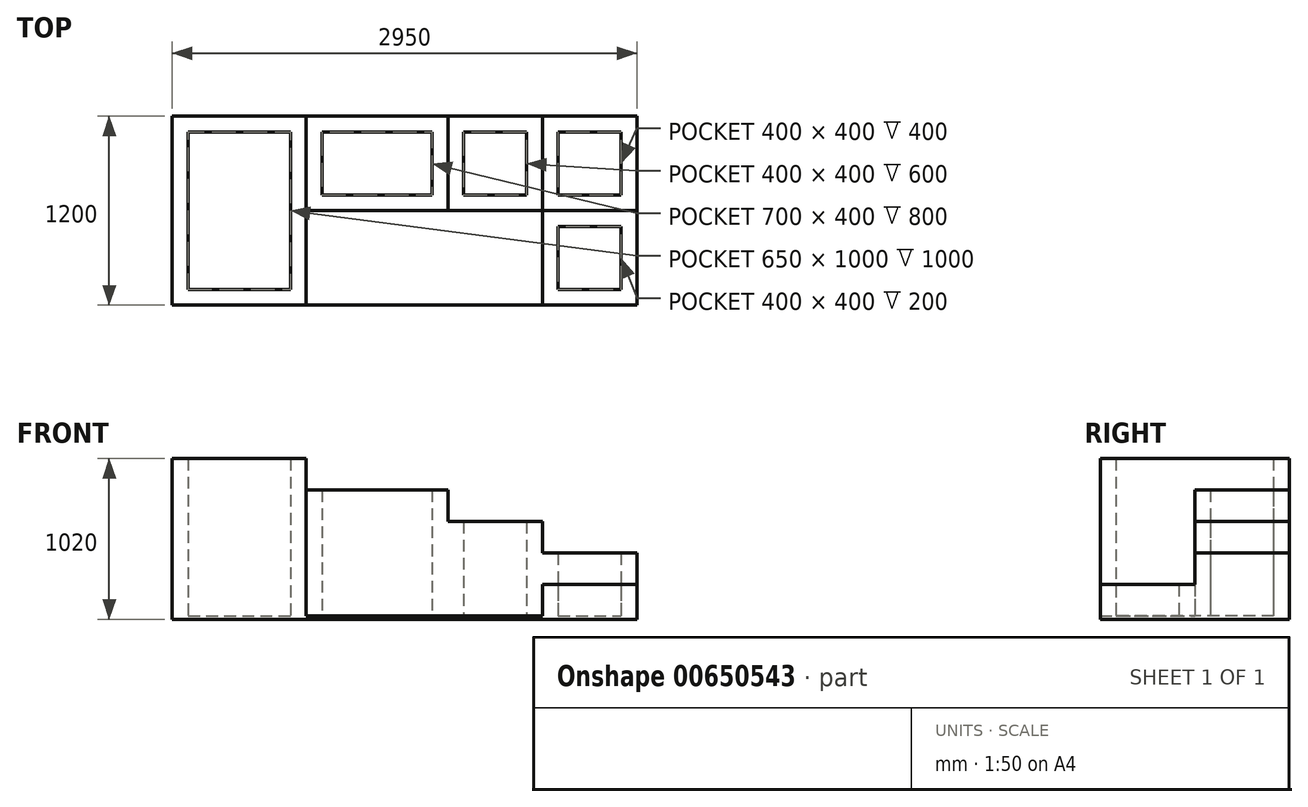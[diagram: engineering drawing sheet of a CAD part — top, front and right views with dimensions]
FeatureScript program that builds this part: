
annotation { "Feature Type Name" : "Feature", "Feature Type Description" : "" }
export const myFeature = defineFeature(function(context is Context, id is Id, definition is map)
    precondition{}
    {
        {
            var Q0;
            Q0=qCreatedBy(makeId("Top.planeOp"),FACE);
            var sketch = newSketch(context, id + "F0", { "sketchPlane" : qUnion([Q0])});
            skLineSegment(sketch, "E0.bottom", {"start": v(0, 0) * mm, "end": v(-2563.64, 0) * mm});
            skLineSegment(sketch, "E0.top", {"start": v(0, 1200) * mm, "end": v(-2950, 1200) * mm});
            skLineSegment(sketch, "E0.left", {"start": v(0, 0) * mm, "end": v(0, 1200) * mm});
            skLineSegment(sketch, "E0.right", {"start": v(-2950, 0) * mm, "end": v(-2950, 1200) * mm});
            skLineSegment(sketch, "E1", {"start": v(-2563.64, 0) * mm, "end": v(-2950, 0) * mm});
            skSolve(sketch);
        }
        {
            var Q0;
            Q0=makeQuery(id+"F0.imprint","IMPRINT",FACE,{"disambiguationData":[TD([[makeQuery(id+"F0.imprint","IMPRINT",EDGE,{"derivedFrom":sQuery(id+"F0.wireOp",EDGE,"E0.bottom")}),-1.0]])]});
            extrude(context, id + "F1", {"entities" : qUnion([Q0]), "depth" : 20 * mm, "offsetDistance" : 25 * mm});
        }
        {
            var Q0;
            Q0=makeQuery(id+"F1.opExtrude","CAP_FACE",FACE,{"disambiguationData":[OSD([sQuery(id+"F0.wireOp",EDGE,"E0.bottom"),sQuery(id+"F0.wireOp",EDGE,"E0.top"),sQuery(id+"F0.wireOp",EDGE,"E0.left"),sQuery(id+"F0.wireOp",EDGE,"E0.right"),sQuery(id+"F0.wireOp",EDGE,"EcOLhzoJ-yrHA-FEvU-6dDI-CAjuHtf4V0fh.bottom"),sQuery(id+"F0.wireOp",EDGE,"EcOLhzoJ-yrHA-FEvU-6dDI-CAjuHtf4V0fh.top"),sQuery(id+"F0.wireOp",EDGE,"EcOLhzoJ-yrHA-FEvU-6dDI-CAjuHtf4V0fh.left"),sQuery(id+"F0.wireOp",EDGE,"EcOLhzoJ-yrHA-FEvU-6dDI-CAjuHtf4V0fh.right")])],"isStart":false});
            var sketch = newSketch(context, id + "F2", { "sketchPlane" : qUnion([Q0])});
            skLineSegment(sketch, "E2.bottom", {"start": v(0, 1200) * mm, "end": v(-600, 1200) * mm});
            skLineSegment(sketch, "E2.top", {"start": v(0, 600) * mm, "end": v(-600, 600) * mm});
            skLineSegment(sketch, "E2.left", {"start": v(0, 1200) * mm, "end": v(0, 600) * mm});
            skLineSegment(sketch, "E2.right", {"start": v(-600, 1200) * mm, "end": v(-600, 600) * mm});
            skLineSegment(sketch, "E3.bottom", {"start": v(-500, 1100) * mm, "end": v(-100, 1100) * mm});
            skLineSegment(sketch, "E3.top", {"start": v(-500, 700) * mm, "end": v(-100, 700) * mm});
            skLineSegment(sketch, "E3.left", {"start": v(-500, 1100) * mm, "end": v(-500, 700) * mm});
            skLineSegment(sketch, "E3.right", {"start": v(-100, 1100) * mm, "end": v(-100, 700) * mm});
            skSolve(sketch);
        }
        {
            var Q0;
            Q0=qSketchRegion(id+"F2",true);
            extrude(context, id + "F3", {"entities" : qUnion([Q0]), "operationType" : NewBodyOperationType.ADD, "depth" : 400 * mm, "offsetDistance" : 25 * mm});
        }
        {
            var Q0;
            {var subQ0=sQuery(id+"F0.wireOp",EDGE,"E0.left");var subQ1=sQuery(id+"F0.wireOp",EDGE,"EcOLhzoJ-yrHA-FEvU-6dDI-CAjuHtf4V0fh.right");var subQ2=sQuery(id+"F0.wireOp",EDGE,"EcOLhzoJ-yrHA-FEvU-6dDI-CAjuHtf4V0fh.left");var subQ3=sQuery(id+"F0.wireOp",EDGE,"EcOLhzoJ-yrHA-FEvU-6dDI-CAjuHtf4V0fh.top");var subQ4=sQuery(id+"F0.wireOp",EDGE,"EcOLhzoJ-yrHA-FEvU-6dDI-CAjuHtf4V0fh.bottom");var subQ5=sQuery(id+"F0.wireOp",EDGE,"E0.bottom");var subQ6=sQuery(id+"F0.wireOp",EDGE,"E0.right");var subQ7=sQuery(id+"F0.wireOp",EDGE,"E0.top");Q0=makeQuery(id+"F3.boolean.opBoolean","SPLIT",FACE,{"disambiguationData":[TD([makeQuery(id+"F1.opExtrude","SWEPT_FACE",FACE,{"disambiguationData":[OSD([subQ5])]})])],"derivedFrom":makeQuery(id+"F1.opExtrude","CAP_FACE",FACE,{"disambiguationData":[OSD([subQ5,subQ7,subQ0,subQ6,subQ4,subQ3,subQ2,subQ1])],"isStart":false})});}
            var sketch = newSketch(context, id + "F4", { "sketchPlane" : qUnion([Q0])});
            skLineSegment(sketch, "E4.bottom", {"start": v(-600, 600) * mm, "end": v(-1200, 600) * mm});
            skLineSegment(sketch, "E4.top", {"start": v(-600, 1200) * mm, "end": v(-1200, 1200) * mm});
            skLineSegment(sketch, "E4.left", {"start": v(-600, 600) * mm, "end": v(-600, 1200) * mm});
            skLineSegment(sketch, "E4.right", {"start": v(-1200, 600) * mm, "end": v(-1200, 1200) * mm});
            skLineSegment(sketch, "E5.bottom", {"start": v(-700, 700) * mm, "end": v(-1100, 700) * mm});
            skLineSegment(sketch, "E5.top", {"start": v(-700, 1100) * mm, "end": v(-1100, 1100) * mm});
            skLineSegment(sketch, "E5.left", {"start": v(-700, 700) * mm, "end": v(-700, 1100) * mm});
            skLineSegment(sketch, "E5.right", {"start": v(-1100, 700) * mm, "end": v(-1100, 1100) * mm});
            skSolve(sketch);
        }
        {
            var Q0;
            Q0=qSketchRegion(id+"F4",true);
            extrude(context, id + "F5", {"entities" : qUnion([Q0]), "operationType" : NewBodyOperationType.ADD, "depth" : 600 * mm, "offsetDistance" : 25 * mm});
        }
        {
            var Q0;
            {var subQ1=sQuery(id+"F0.wireOp",EDGE,"E0.left");var subQ3=sQuery(id+"F0.wireOp",EDGE,"EcOLhzoJ-yrHA-FEvU-6dDI-CAjuHtf4V0fh.right");var subQ5=sQuery(id+"F0.wireOp",EDGE,"EcOLhzoJ-yrHA-FEvU-6dDI-CAjuHtf4V0fh.left");var subQ8=sQuery(id+"F0.wireOp",EDGE,"EcOLhzoJ-yrHA-FEvU-6dDI-CAjuHtf4V0fh.top");var subQ11=sQuery(id+"F0.wireOp",EDGE,"EcOLhzoJ-yrHA-FEvU-6dDI-CAjuHtf4V0fh.bottom");var subQ13=sQuery(id+"F0.wireOp",EDGE,"E0.bottom");var subQ14=makeQuery(id+"F1.opExtrude","SWEPT_FACE",FACE,{"disambiguationData":[OSD([subQ13])]});var subQ15=sQuery(id+"F0.wireOp",EDGE,"E0.right");var subQ17=sQuery(id+"F0.wireOp",EDGE,"E0.top");Q0=makeQuery(id+"F5.boolean.opBoolean","SPLIT",FACE,{"disambiguationData":[TD([subQ14])],"derivedFrom":makeQuery(id+"F3.boolean.opBoolean","SPLIT",FACE,{"disambiguationData":[TD([subQ14])],"derivedFrom":makeQuery(id+"F1.opExtrude","CAP_FACE",FACE,{"disambiguationData":[OSD([subQ13,subQ17,subQ1,subQ15,subQ11,subQ8,subQ5,subQ3])],"isStart":false})})});}
            var sketch = newSketch(context, id + "F6", { "sketchPlane" : qUnion([Q0])});
            skLineSegment(sketch, "E6.bottom", {"start": v(-1200, 600) * mm, "end": v(-2100, 600) * mm});
            skLineSegment(sketch, "E6.top", {"start": v(-1200, 1200) * mm, "end": v(-2100, 1200) * mm});
            skLineSegment(sketch, "E6.left", {"start": v(-1200, 600) * mm, "end": v(-1200, 1200) * mm});
            skLineSegment(sketch, "E6.right", {"start": v(-2100, 600) * mm, "end": v(-2100, 1200) * mm});
            skLineSegment(sketch, "E7.bottom", {"start": v(-1300, 700) * mm, "end": v(-2000, 700) * mm});
            skLineSegment(sketch, "E7.top", {"start": v(-1300, 1100) * mm, "end": v(-2000, 1100) * mm});
            skLineSegment(sketch, "E7.left", {"start": v(-1300, 700) * mm, "end": v(-1300, 1100) * mm});
            skLineSegment(sketch, "E7.right", {"start": v(-2000, 700) * mm, "end": v(-2000, 1100) * mm});
            skSolve(sketch);
        }
        {
            var Q0;
            Q0=qSketchRegion(id+"F6",true);
            extrude(context, id + "F7", {"entities" : qUnion([Q0]), "operationType" : NewBodyOperationType.ADD, "depth" : 800 * mm, "offsetDistance" : 25 * mm});
        }
        {
            var Q0;
            {var subQ1=sQuery(id+"F0.wireOp",EDGE,"E0.left");var subQ3=sQuery(id+"F0.wireOp",EDGE,"EcOLhzoJ-yrHA-FEvU-6dDI-CAjuHtf4V0fh.right");var subQ5=sQuery(id+"F0.wireOp",EDGE,"EcOLhzoJ-yrHA-FEvU-6dDI-CAjuHtf4V0fh.left");var subQ8=sQuery(id+"F0.wireOp",EDGE,"EcOLhzoJ-yrHA-FEvU-6dDI-CAjuHtf4V0fh.top");var subQ11=sQuery(id+"F0.wireOp",EDGE,"EcOLhzoJ-yrHA-FEvU-6dDI-CAjuHtf4V0fh.bottom");var subQ13=sQuery(id+"F0.wireOp",EDGE,"E0.bottom");var subQ14=makeQuery(id+"F1.opExtrude","SWEPT_FACE",FACE,{"disambiguationData":[OSD([subQ13])]});var subQ15=sQuery(id+"F0.wireOp",EDGE,"E0.right");var subQ17=sQuery(id+"F0.wireOp",EDGE,"E0.top");Q0=makeQuery(id+"F7.boolean.opBoolean","SPLIT",FACE,{"disambiguationData":[TD([subQ14])],"derivedFrom":makeQuery(id+"F5.boolean.opBoolean","SPLIT",FACE,{"disambiguationData":[TD([subQ14])],"derivedFrom":makeQuery(id+"F3.boolean.opBoolean","SPLIT",FACE,{"disambiguationData":[TD([subQ14])],"derivedFrom":makeQuery(id+"F1.opExtrude","CAP_FACE",FACE,{"disambiguationData":[OSD([subQ13,subQ17,subQ1,subQ15,subQ11,subQ8,subQ5,subQ3])],"isStart":false})})})});}
            var sketch = newSketch(context, id + "F8", { "sketchPlane" : qUnion([Q0])});
            skLineSegment(sketch, "E8.bottom", {"start": v(-2950, 1200) * mm, "end": v(-2100, 1200) * mm});
            skLineSegment(sketch, "E8.top", {"start": v(-2950, 0) * mm, "end": v(-2100, 0) * mm});
            skLineSegment(sketch, "E8.left", {"start": v(-2950, 1200) * mm, "end": v(-2950, 0) * mm});
            skLineSegment(sketch, "E8.right", {"start": v(-2100, 1200) * mm, "end": v(-2100, 0) * mm});
            skLineSegment(sketch, "E9.bottom", {"start": v(-2850, 1100) * mm, "end": v(-2200, 1100) * mm});
            skLineSegment(sketch, "E9.top", {"start": v(-2850, 100) * mm, "end": v(-2200, 100) * mm});
            skLineSegment(sketch, "E9.left", {"start": v(-2850, 1100) * mm, "end": v(-2850, 100) * mm});
            skLineSegment(sketch, "E9.right", {"start": v(-2200, 1100) * mm, "end": v(-2200, 100) * mm});
            skSolve(sketch);
        }
        {
            var Q0;
            Q0=qSketchRegion(id+"F8",true);
            extrude(context, id + "F9", {"entities" : qUnion([Q0]), "operationType" : NewBodyOperationType.ADD, "depth" : 1000 * mm, "offsetDistance" : 25 * mm});
        }
        {
            var Q0;
            {var subQ1=sQuery(id+"F0.wireOp",EDGE,"EcOLhzoJ-yrHA-FEvU-6dDI-CAjuHtf4V0fh.top");var subQ5=sQuery(id+"F0.wireOp",EDGE,"EcOLhzoJ-yrHA-FEvU-6dDI-CAjuHtf4V0fh.left");var subQ7=sQuery(id+"F0.wireOp",EDGE,"EcOLhzoJ-yrHA-FEvU-6dDI-CAjuHtf4V0fh.right");var subQ9=sQuery(id+"F0.wireOp",EDGE,"E1");var subQ10=sQuery(id+"F0.wireOp",EDGE,"E0.bottom");var subQ12=sQuery(id+"F0.wireOp",EDGE,"E0.left");var subQ13=makeQuery(id+"F1.opExtrude","SWEPT_FACE",FACE,{"disambiguationData":[OSD([subQ12])]});var subQ15=sQuery(id+"F0.wireOp",EDGE,"EcOLhzoJ-yrHA-FEvU-6dDI-CAjuHtf4V0fh.bottom");var subQ18=sQuery(id+"F0.wireOp",EDGE,"E0.top");var subQ19=makeQuery(id+"F1.opExtrude","SWEPT_FACE",FACE,{"disambiguationData":[OSD([subQ18])]});var subQ20=sQuery(id+"F0.wireOp",EDGE,"E0.right");Q0=makeQuery(id+"F9.boolean.opBoolean","SPLIT",FACE,{"disambiguationData":[TD([subQ13])],"derivedFrom":makeQuery(id+"F7.boolean.opBoolean","SPLIT",FACE,{"disambiguationData":[TD([subQ19])],"derivedFrom":makeQuery(id+"F5.boolean.opBoolean","SPLIT",FACE,{"disambiguationData":[TD([subQ19])],"derivedFrom":makeQuery(id+"F3.boolean.opBoolean","SPLIT",FACE,{"disambiguationData":[TD([subQ19])],"derivedFrom":makeQuery(id+"F1.opExtrude","CAP_FACE",FACE,{"disambiguationData":[OSD([subQ10,subQ18,subQ12,subQ20,subQ15,subQ1,subQ5,subQ7,subQ9])],"isStart":false})})})})});}
            var sketch = newSketch(context, id + "F10", { "sketchPlane" : qUnion([Q0])});
            skLineSegment(sketch, "E10.bottom", {"start": v(0, 0) * mm, "end": v(-600, 0) * mm});
            skLineSegment(sketch, "E10.top", {"start": v(0, 600) * mm, "end": v(-600, 600) * mm});
            skLineSegment(sketch, "E10.left", {"start": v(0, 0) * mm, "end": v(0, 600) * mm});
            skLineSegment(sketch, "E10.right", {"start": v(-600, 0) * mm, "end": v(-600, 600) * mm});
            skLineSegment(sketch, "E11.bottom", {"start": v(-100, 100) * mm, "end": v(-500, 100) * mm});
            skLineSegment(sketch, "E11.top", {"start": v(-100, 500) * mm, "end": v(-500, 500) * mm});
            skLineSegment(sketch, "E11.left", {"start": v(-100, 100) * mm, "end": v(-100, 500) * mm});
            skLineSegment(sketch, "E11.right", {"start": v(-500, 100) * mm, "end": v(-500, 500) * mm});
            skSolve(sketch);
        }
        {
            var Q0;
            Q0 = qSketchRegion(id + "F10", true);
            extrude(context, id + "F11", {"entities" : qUnion([Q0]), "operationType" : NewBodyOperationType.ADD, "depth" : 200 * mm, "offsetDistance" : 25 * mm});
        }
    });
